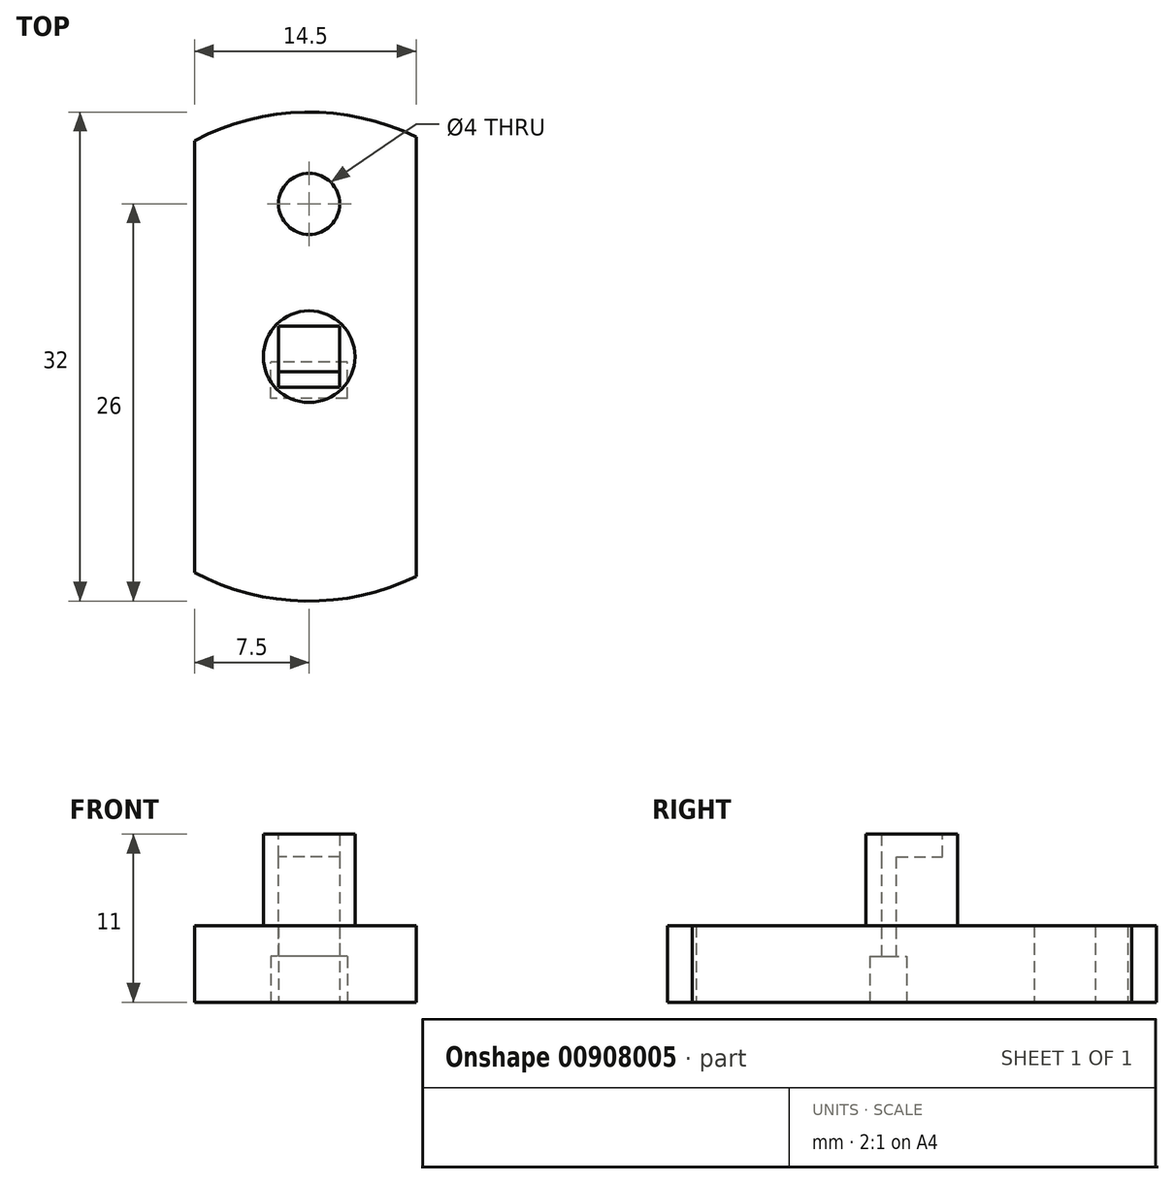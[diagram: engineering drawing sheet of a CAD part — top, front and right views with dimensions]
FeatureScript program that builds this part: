
annotation { "Feature Type Name" : "Feature", "Feature Type Description" : "" }
export const myFeature = defineFeature(function(context is Context, id is Id, definition is map)
    precondition{}
    {
        {
            var Q0;
            Q0=qCreatedBy(makeId("Top.planeOp"),FACE);
            var sketch = newSketch(context, id + "F0", { "sketchPlane" : qUnion([Q0])});
            skCircle(sketch, "E0", {"center": v(0, 0) * mm, "radius": 16 * mm});
            skSolve(sketch);
        }
        {
            var Q0;
            Q0 = qSketchRegion(id + "F0", true);
            extrude(context, id + "F1", {"entities" : qUnion([Q0]), "depth" : 5 * mm, "offsetDistance" : 25 * mm});
        }
        {
            var Q0;
            Q0=makeQuery(id+"F1.opExtrude","CAP_FACE",FACE,{"disambiguationData":[OSD([sQuery(id+"F0.wireOp",EDGE,"E0")])],"isStart":false});
            var sketch = newSketch(context, id + "F2", { "sketchPlane" : qUnion([Q0])});
            skCircle(sketch, "E1", {"center": v(0, 0) * mm, "radius": 3 * mm});
            skSolve(sketch);
        }
        {
            var Q0;
            Q0 = qSketchRegion(id + "F2", true);
            extrude(context, id + "F3", {"entities" : qUnion([Q0]), "operationType" : NewBodyOperationType.ADD, "depth" : 6 * mm, "offsetDistance" : 25 * mm});
        }
        {
            var Q0;
            Q0=makeQuery(id+"F3.opExtrude","CAP_FACE",FACE,{"disambiguationData":[OSD([sQuery(id+"F2.wireOp",EDGE,"E1")])],"isStart":false});
            var sketch = newSketch(context, id + "F4", { "sketchPlane" : qUnion([Q0])});
            skLineSegment(sketch, "E2.bottom", {"start": v(2, -2) * mm, "end": v(-2, -2) * mm});
            skLineSegment(sketch, "E2.top", {"start": v(2, 2) * mm, "end": v(-2, 2) * mm});
            skLineSegment(sketch, "E2.left", {"start": v(2, -2) * mm, "end": v(2, 2) * mm});
            skLineSegment(sketch, "E2.right", {"start": v(-2, -2) * mm, "end": v(-2, 2) * mm});
            skPoint(sketch, "E2.middle", {"position": v(0, 0) * mm});
            skSolve(sketch);
        }
        {
            var Q0;
            Q0 = qSketchRegion(id + "F4", true);
            extrude(context, id + "F5", {"entities" : qUnion([Q0]), "operationType" : NewBodyOperationType.REMOVE, "oppositeDirection" : true, "depth" : 1.5 * mm, "offsetDistance" : 25 * mm});
        }
        {
            var Q0;
            Q0=makeQuery(id+"F3.opExtrude","CAP_FACE",FACE,{"disambiguationData":[OSD([sQuery(id+"F2.wireOp",EDGE,"E1")])],"isStart":false});
            var sketch = newSketch(context, id + "F6", { "sketchPlane" : qUnion([Q0])});
            skLineSegment(sketch, "E3", {"start": v(0, -2) * mm, "end": v(0, -1.5) * mm, "construction": true});
            skLineSegment(sketch, "E4.bottom", {"start": v(2, -1) * mm, "end": v(-2, -1) * mm});
            skLineSegment(sketch, "E4.top", {"start": v(2, -2) * mm, "end": v(-2, -2) * mm});
            skLineSegment(sketch, "E4.left", {"start": v(2, -1) * mm, "end": v(2, -2) * mm});
            skLineSegment(sketch, "E4.right", {"start": v(-2, -1) * mm, "end": v(-2, -2) * mm});
            skPoint(sketch, "E4.middle", {"position": v(0, -1.5) * mm});
            skSolve(sketch);
        }
        {
            var Q0;
            Q0 = qSketchRegion(id + "F6", true);
            extrude(context, id + "F7", {"entities" : qUnion([Q0]), "operationType" : NewBodyOperationType.REMOVE, "oppositeDirection" : true, "depth" : 12 * mm, "offsetDistance" : 25 * mm});
        }
        {
            var Q0;
            Q0=makeQuery(id+"F1.opExtrude","CAP_FACE",FACE,{"disambiguationData":[OSD([sQuery(id+"F0.wireOp",EDGE,"E0")])],"isStart":false});
            var sketch = newSketch(context, id + "F8", { "sketchPlane" : qUnion([Q0])});
            skLineSegment(sketch, "E5", {"start": v(0, 0) * mm, "end": v(0, 10) * mm, "construction": true});
            skCircle(sketch, "E6", {"center": v(0, 10) * mm, "radius": 2 * mm});
            skSolve(sketch);
        }
        {
            var Q0;
            Q0=makeQuery(id+"F1.opExtrude","CAP_FACE",FACE,{"disambiguationData":[OSD([sQuery(id+"F0.wireOp",EDGE,"E0")])],"isStart":true});
            var sketch = newSketch(context, id + "F9", { "sketchPlane" : qUnion([Q0])});
            skLineSegment(sketch, "E7", {"start": v(0, 0) * mm, "end": v(0, -10) * mm});
            skCircle(sketch, "E8", {"center": v(0, -10) * mm, "radius": 2 * mm});
            skSolve(sketch);
        }
        {
            var Q0;
            Q0 = qSketchRegion(id + "F9", true);
            extrude(context, id + "F10", {"entities" : qUnion([Q0]), "operationType" : NewBodyOperationType.REMOVE, "oppositeDirection" : true, "depth" : 5 * mm, "offsetDistance" : 25 * mm});
        }
        {
            var Q0;
            Q0=makeQuery(id+"F8.imprint","IMPRINT",FACE,{"disambiguationData":[TD([[makeQuery(id+"F8.imprint","IMPRINT",EDGE,{"derivedFrom":sQuery(id+"F8.wireOp",EDGE,"E6")}),-1.0]])]});
            var sketch = newSketch(context, id + "F11", { "sketchPlane" : qUnion([Q0])});
            skLineSegment(sketch, "E9", {"start": v(0, 0) * mm, "end": v(15, 0) * mm});
            skLineSegment(sketch, "E10.bottom", {"start": v(7, -17.14) * mm, "end": v(23, -17.14) * mm});
            skLineSegment(sketch, "E10.top", {"start": v(7, 17.14) * mm, "end": v(23, 17.14) * mm});
            skLineSegment(sketch, "E10.left", {"start": v(7, -17.14) * mm, "end": v(7, 17.14) * mm});
            skLineSegment(sketch, "E10.right", {"start": v(23, -17.14) * mm, "end": v(23, 17.14) * mm});
            skPoint(sketch, "E10.middle", {"position": v(15, 0) * mm});
            skSolve(sketch);
        }
        {
            var Q0;
            Q0 = qSketchRegion(id + "F11", true);
            extrude(context, id + "F12", {"entities" : qUnion([Q0]), "operationType" : NewBodyOperationType.REMOVE, "oppositeDirection" : true, "depth" : 10 * mm, "offsetDistance" : 25 * mm});
        }
        {
            var Q0;
            Q0=makeQuery(id+"F8.imprint","IMPRINT",FACE,{"disambiguationData":[TD([[makeQuery(id+"F8.imprint","IMPRINT",EDGE,{"derivedFrom":sQuery(id+"F8.wireOp",EDGE,"E6")}),-1.0]])]});
            var sketch = newSketch(context, id + "F13", { "sketchPlane" : qUnion([Q0])});
            skLineSegment(sketch, "E11", {"start": v(0, 0) * mm, "end": v(-15, 0) * mm});
            skLineSegment(sketch, "E12.bottom", {"start": v(-7.5, -25.13) * mm, "end": v(-22.5, -25.13) * mm});
            skLineSegment(sketch, "E12.top", {"start": v(-7.5, 25.13) * mm, "end": v(-22.5, 25.13) * mm});
            skLineSegment(sketch, "E12.left", {"start": v(-7.5, -25.13) * mm, "end": v(-7.5, 25.13) * mm});
            skLineSegment(sketch, "E12.right", {"start": v(-22.5, -25.13) * mm, "end": v(-22.5, 25.13) * mm});
            skPoint(sketch, "E12.middle", {"position": v(-15, 0) * mm});
            skPoint(sketch, "E12.cornerSnap0", {"position": v(-7.5, 0) * mm});
            skSolve(sketch);
        }
        {
            var Q0;
            Q0 = qSketchRegion(id + "F13", true);
            extrude(context, id + "F14", {"entities" : qUnion([Q0]), "operationType" : NewBodyOperationType.REMOVE, "oppositeDirection" : true, "depth" : 10 * mm, "offsetDistance" : 25 * mm});
        }
        {
            var Q0;
            Q0=makeQuery(id+"F1.opExtrude","CAP_FACE",FACE,{"disambiguationData":[OSD([sQuery(id+"F0.wireOp",EDGE,"E0")])],"isStart":true});
            var sketch = newSketch(context, id + "F15", { "sketchPlane" : qUnion([Q0])});
            skLineSegment(sketch, "E13.bottom", {"start": v(2.5, 2.75) * mm, "end": v(-2.5, 2.75) * mm});
            skLineSegment(sketch, "E13.top", {"start": v(2.5, 0.35) * mm, "end": v(-2.5, 0.35) * mm});
            skLineSegment(sketch, "E13.left", {"start": v(2.5, 2.75) * mm, "end": v(2.5, 0.35) * mm});
            skLineSegment(sketch, "E13.right", {"start": v(-2.5, 2.75) * mm, "end": v(-2.5, 0.35) * mm});
            skPoint(sketch, "E13.middle", {"position": v(0, 1.55) * mm});
            skPoint(sketch, "E13.middle.positionSnap0", {"position": v(0, 2) * mm});
            skPoint(sketch, "E13.centerSnap0", {"position": v(0, 2) * mm});
            skSolve(sketch);
        }
        {
            var Q0;
            Q0 = qSketchRegion(id + "F15", true);
            extrude(context, id + "F16", {"entities" : qUnion([Q0]), "operationType" : NewBodyOperationType.REMOVE, "oppositeDirection" : true, "depth" : 3 * mm, "offsetDistance" : 25 * mm});
        }
    });
